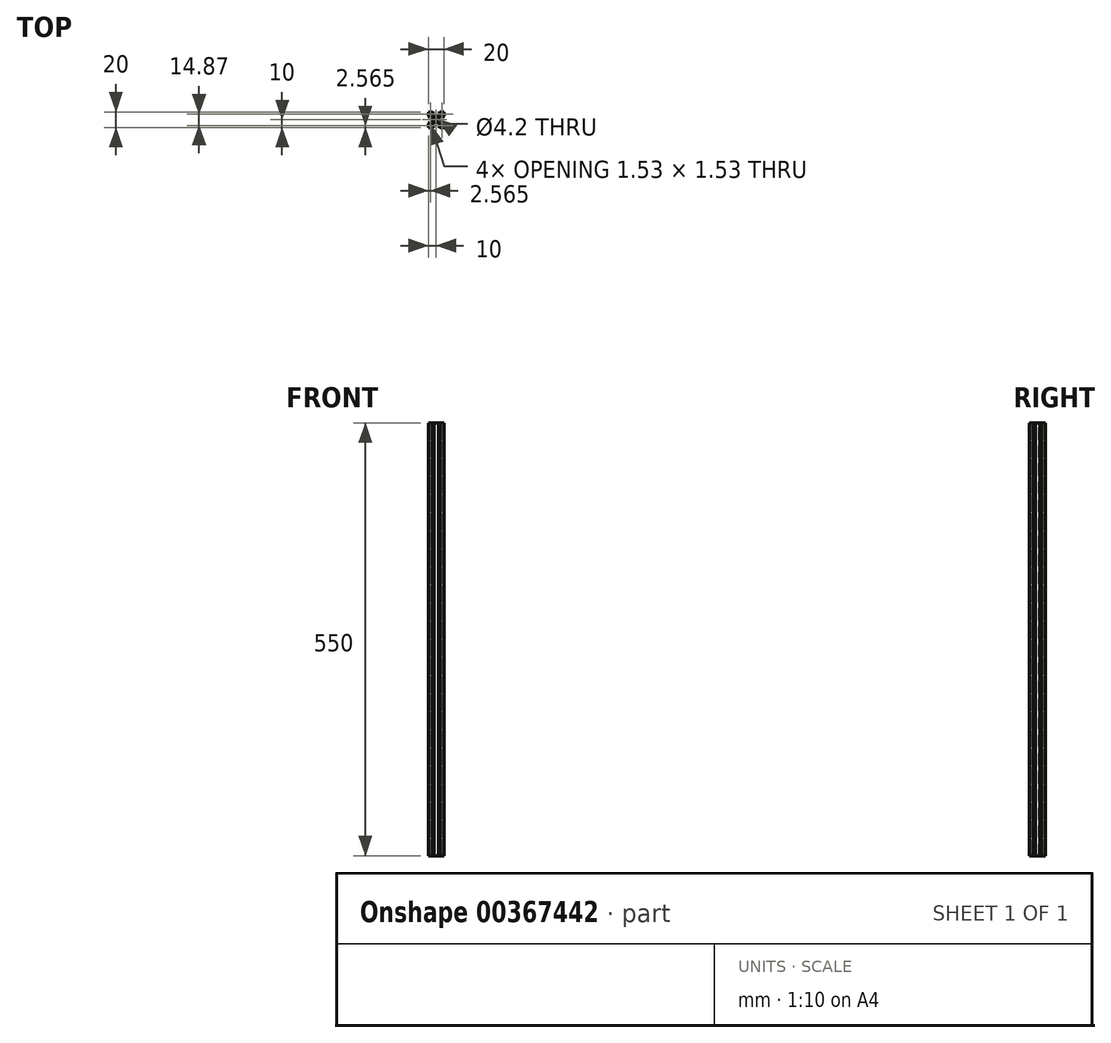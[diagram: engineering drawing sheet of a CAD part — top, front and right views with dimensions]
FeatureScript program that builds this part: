
annotation { "Feature Type Name" : "Feature", "Feature Type Description" : "" }
export const myFeature = defineFeature(function(context is Context, id is Id, definition is map)
    precondition{}
    {
        {
            var Q0;
            Q0=qCreatedBy(makeId("Top.planeOp"),FACE);
            var sketch = newSketch(context, id + "F0", { "sketchPlane" : qUnion([Q0])});
            skLineSegment(sketch, "E0.bottom", {"start": v(0, 0) * mm, "end": v(5.2, 0) * mm});
            skLineSegment(sketch, "E0.top", {"start": v(0, 20) * mm, "end": v(5.2, 20) * mm});
            skLineSegment(sketch, "E0.left", {"start": v(0, 0) * mm, "end": v(0, 5.2) * mm});
            skLineSegment(sketch, "E0.right", {"start": v(20, 0) * mm, "end": v(20, 5.2) * mm});
            skLineSegment(sketch, "E1", {"start": v(20, 5.2) * mm, "end": v(18.2, 7) * mm});
            skLineSegment(sketch, "E2", {"start": v(18.2, 7) * mm, "end": v(18.2, 4.4) * mm});
            skLineSegment(sketch, "E3", {"start": v(18.2, 4.4) * mm, "end": v(16.56, 4.4) * mm});
            skLineSegment(sketch, "E4", {"start": v(16.56, 4.4) * mm, "end": v(13.8, 7.16) * mm});
            skLineSegment(sketch, "E5", {"start": v(13.8, 7.16) * mm, "end": v(13.8, 12.84) * mm});
            skLineSegment(sketch, "E6", {"start": v(13.8, 12.84) * mm, "end": v(16.56, 15.6) * mm});
            skLineSegment(sketch, "E7", {"start": v(16.56, 15.6) * mm, "end": v(18.2, 15.6) * mm});
            skLineSegment(sketch, "E8", {"start": v(18.2, 15.6) * mm, "end": v(18.2, 13) * mm});
            skLineSegment(sketch, "E9", {"start": v(18.2, 13) * mm, "end": v(20, 14.8) * mm});
            skPoint(sketch, "E10.centerSnap0", {"position": v(13.8, 10) * mm});
            skLineSegment(sketch, "E11.trimOffspring", {"start": v(20, 14.8) * mm, "end": v(20, 20) * mm});
            skLineSegment(sketch, "E12", {"start": v(14.8, 20) * mm, "end": v(13, 18.2) * mm});
            skLineSegment(sketch, "E13", {"start": v(13, 18.2) * mm, "end": v(15.6, 18.2) * mm});
            skLineSegment(sketch, "E14", {"start": v(15.6, 18.2) * mm, "end": v(15.6, 16.56) * mm});
            skLineSegment(sketch, "E15", {"start": v(15.6, 16.56) * mm, "end": v(12.84, 13.8) * mm});
            skLineSegment(sketch, "E16", {"start": v(12.84, 13.8) * mm, "end": v(7.16, 13.8) * mm});
            skLineSegment(sketch, "E17", {"start": v(7.16, 13.8) * mm, "end": v(4.4, 16.56) * mm});
            skLineSegment(sketch, "E18", {"start": v(4.4, 16.56) * mm, "end": v(4.4, 18.2) * mm});
            skLineSegment(sketch, "E19", {"start": v(4.4, 18.2) * mm, "end": v(7, 18.2) * mm});
            skLineSegment(sketch, "E20", {"start": v(7, 18.2) * mm, "end": v(5.2, 20) * mm});
            skLineSegment(sketch, "E21.trimOffspring", {"start": v(14.8, 20) * mm, "end": v(20, 20) * mm});
            skLineSegment(sketch, "E22", {"start": v(14.8, 0) * mm, "end": v(13, 1.8) * mm});
            skLineSegment(sketch, "E23", {"start": v(13, 1.8) * mm, "end": v(15.6, 1.8) * mm});
            skLineSegment(sketch, "E24", {"start": v(15.6, 1.8) * mm, "end": v(15.6, 3.44) * mm});
            skLineSegment(sketch, "E25", {"start": v(15.6, 3.44) * mm, "end": v(12.84, 6.2) * mm});
            skLineSegment(sketch, "E26", {"start": v(12.84, 6.2) * mm, "end": v(7.16, 6.2) * mm});
            skLineSegment(sketch, "E27", {"start": v(7.16, 6.2) * mm, "end": v(4.4, 3.44) * mm});
            skLineSegment(sketch, "E28", {"start": v(4.4, 3.44) * mm, "end": v(4.4, 1.8) * mm});
            skLineSegment(sketch, "E29", {"start": v(4.4, 1.8) * mm, "end": v(7, 1.8) * mm});
            skLineSegment(sketch, "E30", {"start": v(7, 1.8) * mm, "end": v(5.2, 0) * mm});
            skLineSegment(sketch, "E31", {"start": v(0, 14.8) * mm, "end": v(1.8, 13) * mm});
            skLineSegment(sketch, "E32", {"start": v(1.8, 13) * mm, "end": v(1.8, 15.6) * mm});
            skLineSegment(sketch, "E33", {"start": v(1.8, 15.6) * mm, "end": v(3.44, 15.6) * mm});
            skLineSegment(sketch, "E34", {"start": v(3.44, 15.6) * mm, "end": v(6.2, 12.84) * mm});
            skLineSegment(sketch, "E35", {"start": v(6.2, 12.84) * mm, "end": v(6.2, 7.16) * mm});
            skLineSegment(sketch, "E36", {"start": v(6.2, 7.16) * mm, "end": v(3.44, 4.4) * mm});
            skLineSegment(sketch, "E37", {"start": v(3.44, 4.4) * mm, "end": v(1.8, 4.4) * mm});
            skLineSegment(sketch, "E38", {"start": v(1.8, 4.4) * mm, "end": v(1.8, 7) * mm});
            skLineSegment(sketch, "E39", {"start": v(1.8, 7) * mm, "end": v(0, 5.2) * mm});
            skLineSegment(sketch, "E40.trimOffspring", {"start": v(0, 14.8) * mm, "end": v(0, 20) * mm});
            skLineSegment(sketch, "E41.trimOffspring", {"start": v(14.8, 0) * mm, "end": v(20, 0) * mm});
            skSolve(sketch);
        }
        {
            var Q0;
            Q0=qSketchRegion(id+"F0",true);
            extrude(context, id + "F1", {"entities" : qUnion([Q0]), "depth" : 550 * mm});
        }
        {
            var Q0;
            Q0=makeQuery(id+"F1.opExtrude","CAP_FACE",FACE,{"disambiguationData":[OSD([sQuery(id+"F0.wireOp",EDGE,"E0.bottom"),sQuery(id+"F0.wireOp",EDGE,"E0.top"),sQuery(id+"F0.wireOp",EDGE,"E0.left"),sQuery(id+"F0.wireOp",EDGE,"E0.right"),sQuery(id+"F0.wireOp",EDGE,"E1"),sQuery(id+"F0.wireOp",EDGE,"E2"),sQuery(id+"F0.wireOp",EDGE,"E3"),sQuery(id+"F0.wireOp",EDGE,"E4"),sQuery(id+"F0.wireOp",EDGE,"E5"),sQuery(id+"F0.wireOp",EDGE,"E6"),sQuery(id+"F0.wireOp",EDGE,"E7"),sQuery(id+"F0.wireOp",EDGE,"E8"),sQuery(id+"F0.wireOp",EDGE,"E9"),sQuery(id+"F0.wireOp",EDGE,"E11.trimOffspring"),sQuery(id+"F0.wireOp",EDGE,"E12"),sQuery(id+"F0.wireOp",EDGE,"E13"),sQuery(id+"F0.wireOp",EDGE,"E14"),sQuery(id+"F0.wireOp",EDGE,"E15"),sQuery(id+"F0.wireOp",EDGE,"E16"),sQuery(id+"F0.wireOp",EDGE,"E17"),sQuery(id+"F0.wireOp",EDGE,"E18"),sQuery(id+"F0.wireOp",EDGE,"E19"),sQuery(id+"F0.wireOp",EDGE,"E20"),sQuery(id+"F0.wireOp",EDGE,"E21.trimOffspring"),sQuery(id+"F0.wireOp",EDGE,"E22"),sQuery(id+"F0.wireOp",EDGE,"E23"),sQuery(id+"F0.wireOp",EDGE,"E24"),sQuery(id+"F0.wireOp",EDGE,"E25"),sQuery(id+"F0.wireOp",EDGE,"E26"),sQuery(id+"F0.wireOp",EDGE,"E27"),sQuery(id+"F0.wireOp",EDGE,"E28"),sQuery(id+"F0.wireOp",EDGE,"E29"),sQuery(id+"F0.wireOp",EDGE,"E30"),sQuery(id+"F0.wireOp",EDGE,"E31"),sQuery(id+"F0.wireOp",EDGE,"E32"),sQuery(id+"F0.wireOp",EDGE,"E33"),sQuery(id+"F0.wireOp",EDGE,"E34"),sQuery(id+"F0.wireOp",EDGE,"E35"),sQuery(id+"F0.wireOp",EDGE,"E36"),sQuery(id+"F0.wireOp",EDGE,"E37"),sQuery(id+"F0.wireOp",EDGE,"E38"),sQuery(id+"F0.wireOp",EDGE,"E39"),sQuery(id+"F0.wireOp",EDGE,"E40.trimOffspring"),sQuery(id+"F0.wireOp",EDGE,"E41.trimOffspring")])],"isStart":false});
            var sketch = newSketch(context, id + "F2", { "sketchPlane" : qUnion([Q0])});
            skCircle(sketch, "E42", {"center": v(10, 10) * mm, "radius": 2.1 * mm});
            skPoint(sketch, "E42.centerSnap0", {"position": v(10, 13.8) * mm});
            skPoint(sketch, "E42.centerSnap1", {"position": v(13.8, 10) * mm});
            skLineSegment(sketch, "E43", {"start": v(18.2, 18.2) * mm, "end": v(16.67, 18.2) * mm});
            skLineSegment(sketch, "E44", {"start": v(16.67, 18.2) * mm, "end": v(18.2, 16.67) * mm});
            skLineSegment(sketch, "E45", {"start": v(18.2, 16.67) * mm, "end": v(18.2, 18.2) * mm});
            skLineSegment(sketch, "E46", {"start": v(1.8, 18.2) * mm, "end": v(1.8, 16.67) * mm});
            skLineSegment(sketch, "E47", {"start": v(1.8, 16.67) * mm, "end": v(3.33, 18.2) * mm});
            skLineSegment(sketch, "E48", {"start": v(3.33, 18.2) * mm, "end": v(1.8, 18.2) * mm});
            skLineSegment(sketch, "E49", {"start": v(1.8, 1.8) * mm, "end": v(3.33, 1.8) * mm});
            skLineSegment(sketch, "E50", {"start": v(3.33, 1.8) * mm, "end": v(1.8, 3.33) * mm});
            skLineSegment(sketch, "E51", {"start": v(1.8, 3.33) * mm, "end": v(1.8, 1.8) * mm});
            skLineSegment(sketch, "E52", {"start": v(18.2, 1.8) * mm, "end": v(18.2, 3.33) * mm});
            skLineSegment(sketch, "E53", {"start": v(18.2, 3.33) * mm, "end": v(16.67, 1.8) * mm});
            skLineSegment(sketch, "E54", {"start": v(16.67, 1.8) * mm, "end": v(18.2, 1.8) * mm});
            skSolve(sketch);
        }
        {
            var Q0;
            Q0=qSketchRegion(id+"F2",true);
            extrude(context, id + "F3", {"entities" : qUnion([Q0]), "operationType" : NewBodyOperationType.REMOVE, "endBound" : BoundingType.THROUGH_ALL, "oppositeDirection" : true, "depth" : 25 * mm});
        }
    });
